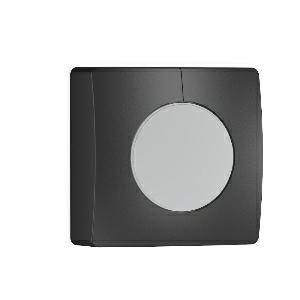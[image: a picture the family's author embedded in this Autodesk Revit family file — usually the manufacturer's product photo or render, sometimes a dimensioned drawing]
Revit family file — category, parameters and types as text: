
# Revit family: nightmatic_5000-3_011680
name_source: partatom
category: Elektroinstallationen
revit_build: Autodesk Revit 2016 (Build: 20190508_0715(x64)
units: mm (PartAtom-declared; Revit-internal decimal feet)

## family parameters
Basisbauteil = Fläche
Beim Laden mit Abzugskörper schneiden = Nein
Bemaßung runder Anschluss = Durchmesser verwenden
Beschriftungsausrichtung beibehalten = Nein
Gemeinsam genutzt = Nein
Raumberechnungspunkt = Nein
Teiletyp = Normal

## types (1)
- NightMatic 5000-3
    Apparent Load = 0 VA
    Beschreibung = Type: Photo-cell controller; Dimensions (L x W x H): 42 x 95 x 95 mm; Mains power supply: 220 – 240 V / 50 – 60 Hz; Sensor Technology: Light sensor; Application, place: Indoors; Installation site: wall, corner; Installation: Surface wiring; Twilight setting: 2 – 1000 lx; Switching output 1, resistive: 2000 W; Switching output 1, number of LEDs / fluorescent lamps: 8 pcs.; Basic light level function: No; Functions: Night economy mode, light ON / OFF in the morning; Settings via: Remote control, Potentiometers, Smart Remote; IP-rating: IP54; Material: Plastic; Ambient temperature: -20 – 50 °C; Colour: black; Colour, RAL: 9005; Manufacturer's Warranty: 5 years; Version: COM1 - black; PU1, EAN: 4007841011680
    Height = 95 mm
    Hersteller = Steinel
    Length = 42 mm
    ModVariant = Nein
    Modell = 011680
    Mounting Type = Surface mounted
    Number of Poles = 1
    OnlyDefault = Ja
    Power Factor = 1
    Product Name = NightMatic 5000-3
    Product group = Sensor-switched indoor light
    ProductGroupID = 30
    Protection Class = Protection class
    Protection Degree = IP 54
    RlxData = <blob elided: 28689 chars, md5=de5a9645>
    SensorDataFile = {"IESDataFiles":[]}
    Typenbild = produkt1_011680.jpg
    Typenkommentare = Product without accessories
    URL = http://relux.com
    VarID = ---
    Voltage = 0 V
    Vorgabe-Ansicht = 1800 mm
    Weight = 0.00 kg
    Width = 95 mm

## geometry (parser evidence)
native form markers: Blend x4, Sweep x12
no freeform markers — native parametric forms only
